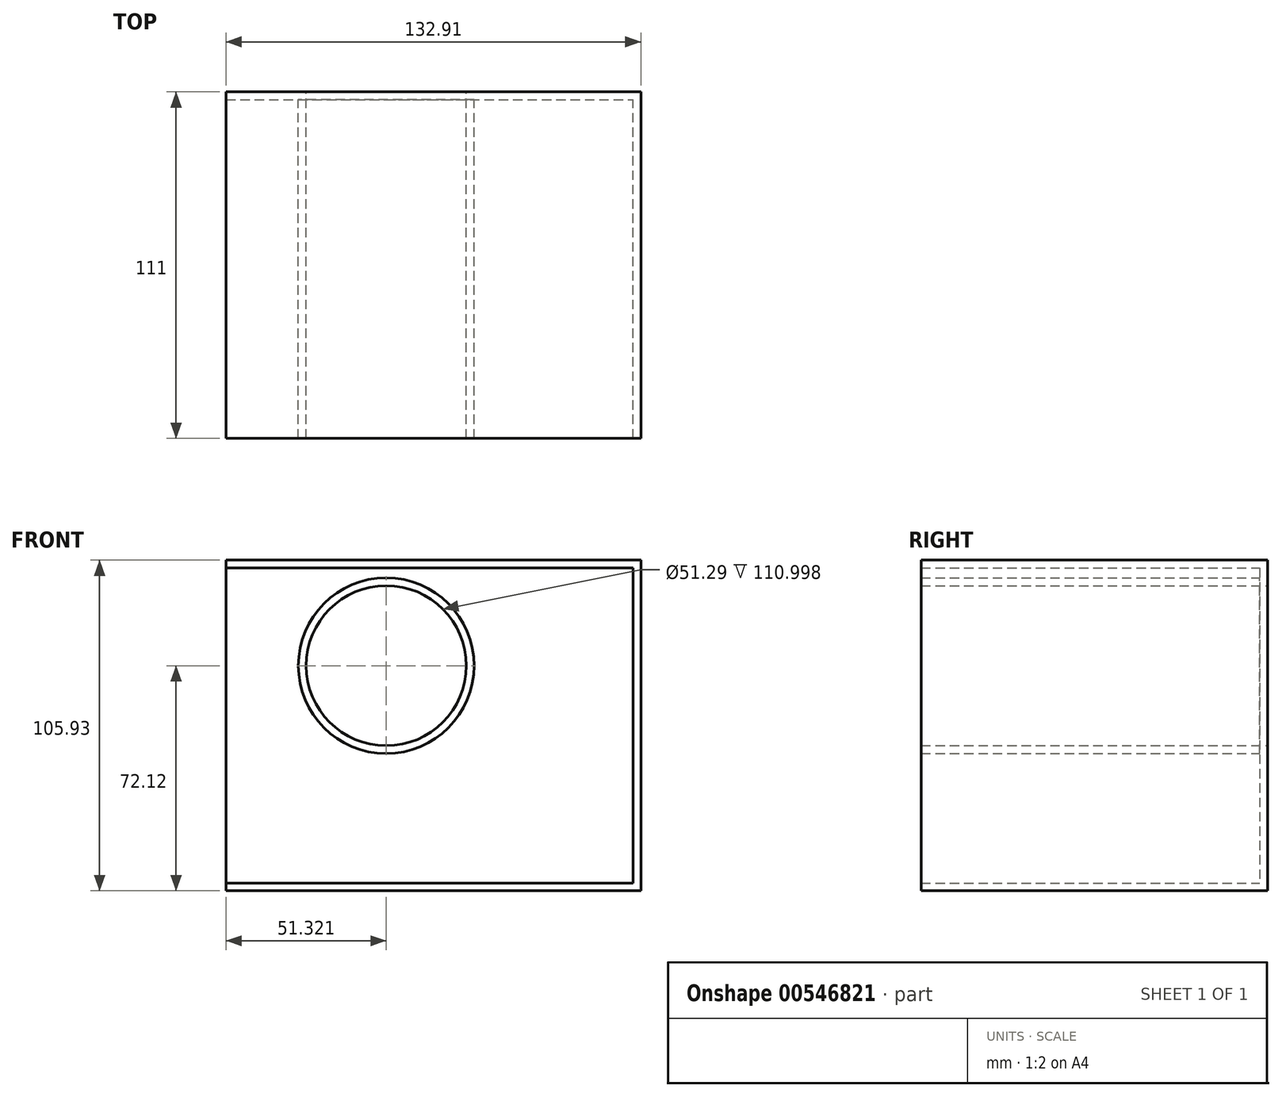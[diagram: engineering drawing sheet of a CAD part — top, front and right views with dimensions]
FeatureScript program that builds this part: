
annotation { "Feature Type Name" : "Feature", "Feature Type Description" : "" }
export const myFeature = defineFeature(function(context is Context, id is Id, definition is map)
    precondition{}
    {
        {
            var Q0;
            Q0=qCreatedBy(makeId("Front.planeOp"),FACE);
            var sketch = newSketch(context, id + "F0", { "sketchPlane" : qUnion([Q0])});
            skLineSegment(sketch, "E0.bottom", {"start": v(-54.77, 51.84) * mm, "end": v(52.74, 51.84) * mm});
            skLineSegment(sketch, "E0.top", {"start": v(-54.77, -54.1) * mm, "end": v(52.74, -54.1) * mm});
            skLineSegment(sketch, "E0.left", {"start": v(-54.77, 51.84) * mm, "end": v(-54.77, -54.1) * mm});
            skLineSegment(sketch, "E0.right", {"start": v(52.74, 51.84) * mm, "end": v(52.74, -54.1) * mm});
            skCircle(sketch, "E1", {"center": v(-28.85, 18.03) * mm, "radius": 25.64 * mm});
            skSolve(sketch);
        }
        {
            var Q0;
            Q0 = qSketchRegion(id + "F0", true);
            extrude(context, id + "F1", {"entities" : qUnion([Q0]), "depth" : 25.4 * mm, "offsetDistance" : 25.4 * mm});
        }
        {
            var Q0;
            Q0=makeQuery(id+"F1.opExtrude","CAP_FACE",FACE,{"disambiguationData":[OSD([sQuery(id+"F0.wireOp",EDGE,"E0.bottom"),sQuery(id+"F0.wireOp",EDGE,"E0.top"),sQuery(id+"F0.wireOp",EDGE,"E0.left"),sQuery(id+"F0.wireOp",EDGE,"E0.right"),sQuery(id+"F0.wireOp",EDGE,"E1")])],"isStart":false});
            var Q1;
            Q1=makeQuery(id+"F1.opExtrude","CAP_FACE",FACE,{"disambiguationData":[OSD([sQuery(id+"F0.wireOp",EDGE,"E0.bottom"),sQuery(id+"F0.wireOp",EDGE,"E0.top"),sQuery(id+"F0.wireOp",EDGE,"E0.left"),sQuery(id+"F0.wireOp",EDGE,"E0.right"),sQuery(id+"F0.wireOp",EDGE,"E1")])],"isStart":true});
            extrude(context, id + "F2", {"entities" : qUnion([Q0, Q1]), "operationType" : NewBodyOperationType.ADD, "depth" : 85.6 * mm, "offsetDistance" : 25.4 * mm});
        }
        {
            var Q0;
            {var subQ0=sQuery(id+"F0.wireOp",EDGE,"E0.left");Q0=makeQuery(id+"F2.boolean.opBoolean","MERGE",FACE,{"derivedFrom":[makeQuery(id+"F1.opExtrude","SWEPT_FACE",FACE,{"disambiguationData":[OSD([subQ0])]}),makeQuery(id+"F2.opExtrude","SWEPT_FACE",FACE,{"disambiguationData":[OSD([subQ0]),TDD([makeQuery(id+"F1.opExtrude","CAP_EDGE",EDGE,{"disambiguationData":[OSD([subQ0])],"isStart":true})])]}),makeQuery(id+"F2.opExtrude","SWEPT_FACE",FACE,{"disambiguationData":[OSD([subQ0]),TDD([makeQuery(id+"F1.opExtrude","CAP_EDGE",EDGE,{"disambiguationData":[OSD([subQ0])],"isStart":false})])]})]});}
            var Q1;
            {var subQ0=sQuery(id+"F0.wireOp",EDGE,"E0.right");Q1=makeQuery(id+"F2.boolean.opBoolean","MERGE",FACE,{"derivedFrom":[makeQuery(id+"F1.opExtrude","SWEPT_FACE",FACE,{"disambiguationData":[OSD([subQ0])]}),makeQuery(id+"F2.opExtrude","SWEPT_FACE",FACE,{"disambiguationData":[OSD([subQ0]),TDD([makeQuery(id+"F1.opExtrude","CAP_EDGE",EDGE,{"disambiguationData":[OSD([subQ0])],"isStart":true})])]}),makeQuery(id+"F2.opExtrude","SWEPT_FACE",FACE,{"disambiguationData":[OSD([subQ0]),TDD([makeQuery(id+"F1.opExtrude","CAP_EDGE",EDGE,{"disambiguationData":[OSD([subQ0])],"isStart":false})])]})]});}
            extrude(context, id + "F3", {"entities" : qUnion([Q0, Q1]), "operationType" : NewBodyOperationType.ADD, "depth" : 25.4 * mm, "offsetDistance" : 25.4 * mm});
        }
        {
            var Q0;
            {var subQ0=sQuery(id+"F0.wireOp",EDGE,"E0.left");var subQ1=sQuery(id+"F0.wireOp",EDGE,"E1");var subQ2=sQuery(id+"F0.wireOp",EDGE,"E0.right");var subQ3=sQuery(id+"F0.wireOp",EDGE,"E0.top");var subQ4=sQuery(id+"F0.wireOp",EDGE,"E0.bottom");Q0=makeQuery(id+"F3.boolean.opBoolean","MERGE",FACE,{"derivedFrom":[makeQuery(id+"F2.opExtrude","CAP_FACE",FACE,{"disambiguationData":[OSD([subQ4,subQ3,subQ0,subQ2,subQ1]),TDD([makeQuery(id+"F1.opExtrude","CAP_FACE",FACE,{"disambiguationData":[OSD([subQ4,subQ3,subQ0,subQ2,subQ1])],"isStart":false})])],"isStart":false}),makeQuery(id+"F3.opExtrude","SWEPT_FACE",FACE,{"disambiguationData":[OSD([subQ0]),TDD([makeQuery(id+"F2.opExtrude","CAP_EDGE",EDGE,{"disambiguationData":[OSD([subQ0]),TDD([makeQuery(id+"F1.opExtrude","CAP_EDGE",EDGE,{"disambiguationData":[OSD([subQ0])],"isStart":false})])],"isStart":false})])]})]});}
            var Q1;
            Q1=makeQuery(id+"F3.opExtrude","CAP_FACE",FACE,{"disambiguationData":[OSD([sQuery(id+"F0.wireOp",EDGE,"E0.left")])],"isStart":false});
            shell(context, id + "F4", {"entities" : qUnion([Q0, Q1]), "thickness" : 2.5 * mm});
        }
    });
